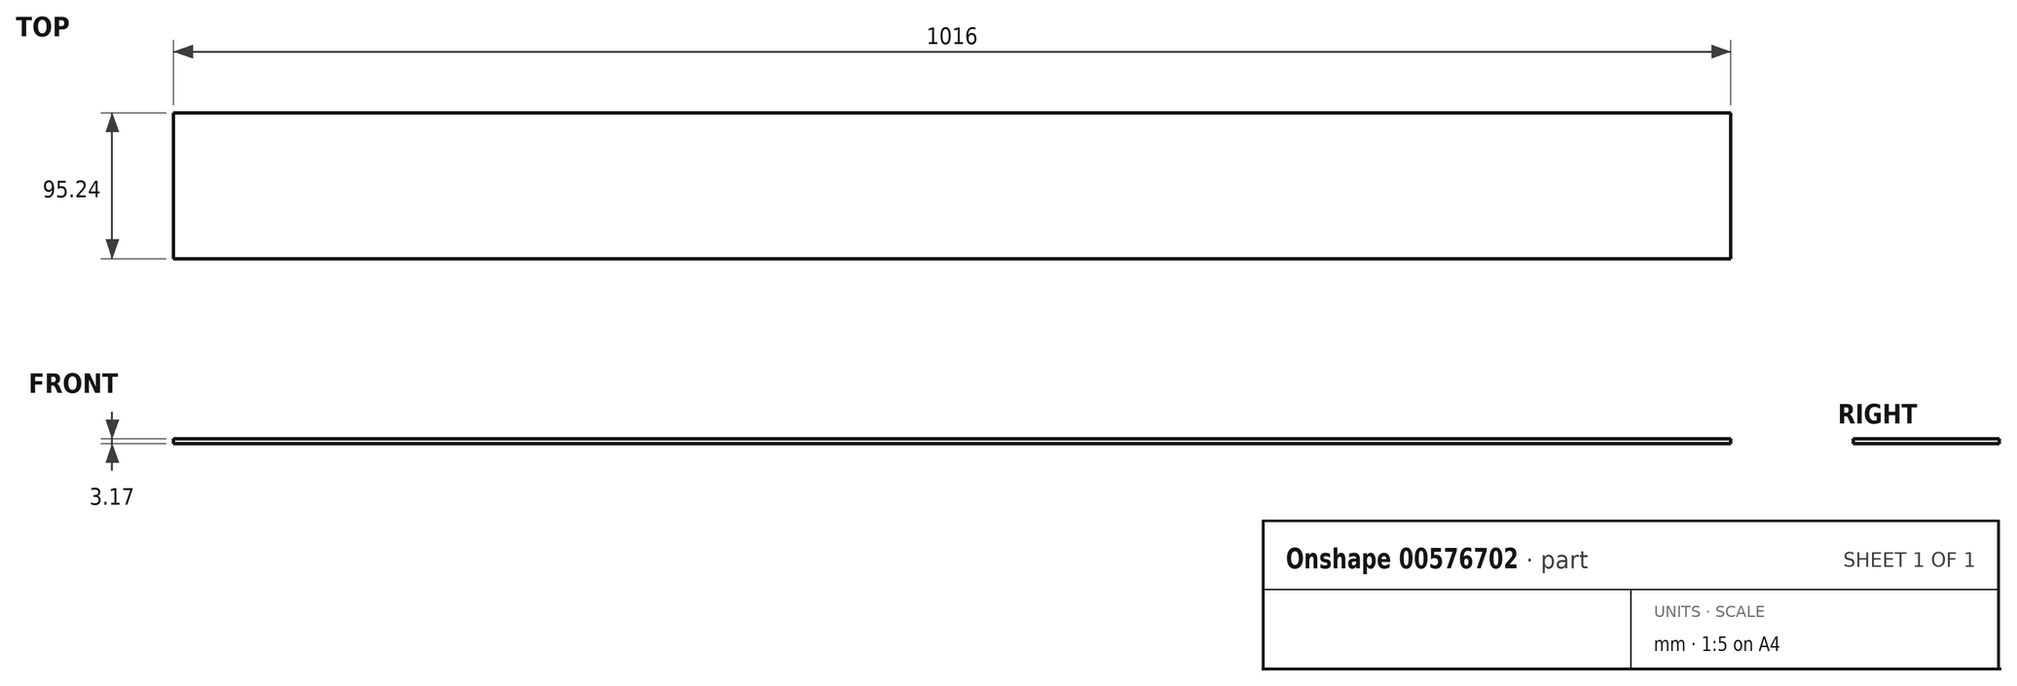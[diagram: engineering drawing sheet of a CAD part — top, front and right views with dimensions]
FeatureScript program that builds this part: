
annotation { "Feature Type Name" : "Feature", "Feature Type Description" : "" }
export const myFeature = defineFeature(function(context is Context, id is Id, definition is map)
    precondition{}
    {
        {
            var Q0;
            Q0=qCreatedBy(makeId("Top.planeOp"),FACE);
            var sketch = newSketch(context, id + "F0", { "sketchPlane" : qUnion([Q0])});
            skLineSegment(sketch, "E0.bottom", {"start": v(508, 47.63) * mm, "end": v(-508, 47.63) * mm});
            skLineSegment(sketch, "E0.top", {"start": v(508, -47.63) * mm, "end": v(-508, -47.63) * mm});
            skLineSegment(sketch, "E0.left", {"start": v(508, 47.63) * mm, "end": v(508, -47.63) * mm});
            skLineSegment(sketch, "E0.right", {"start": v(-508, 47.63) * mm, "end": v(-508, -47.63) * mm});
            skPoint(sketch, "E0.middle", {"position": v(0, 0) * mm});
            skSolve(sketch);
        }
        {
            var Q0;
            Q0 = qSketchRegion(id + "F0", true);
            extrude(context, id + "F1", {"entities" : qUnion([Q0]), "depth" : 3.17 * mm, "offsetDistance" : 25.4 * mm});
        }
    });
